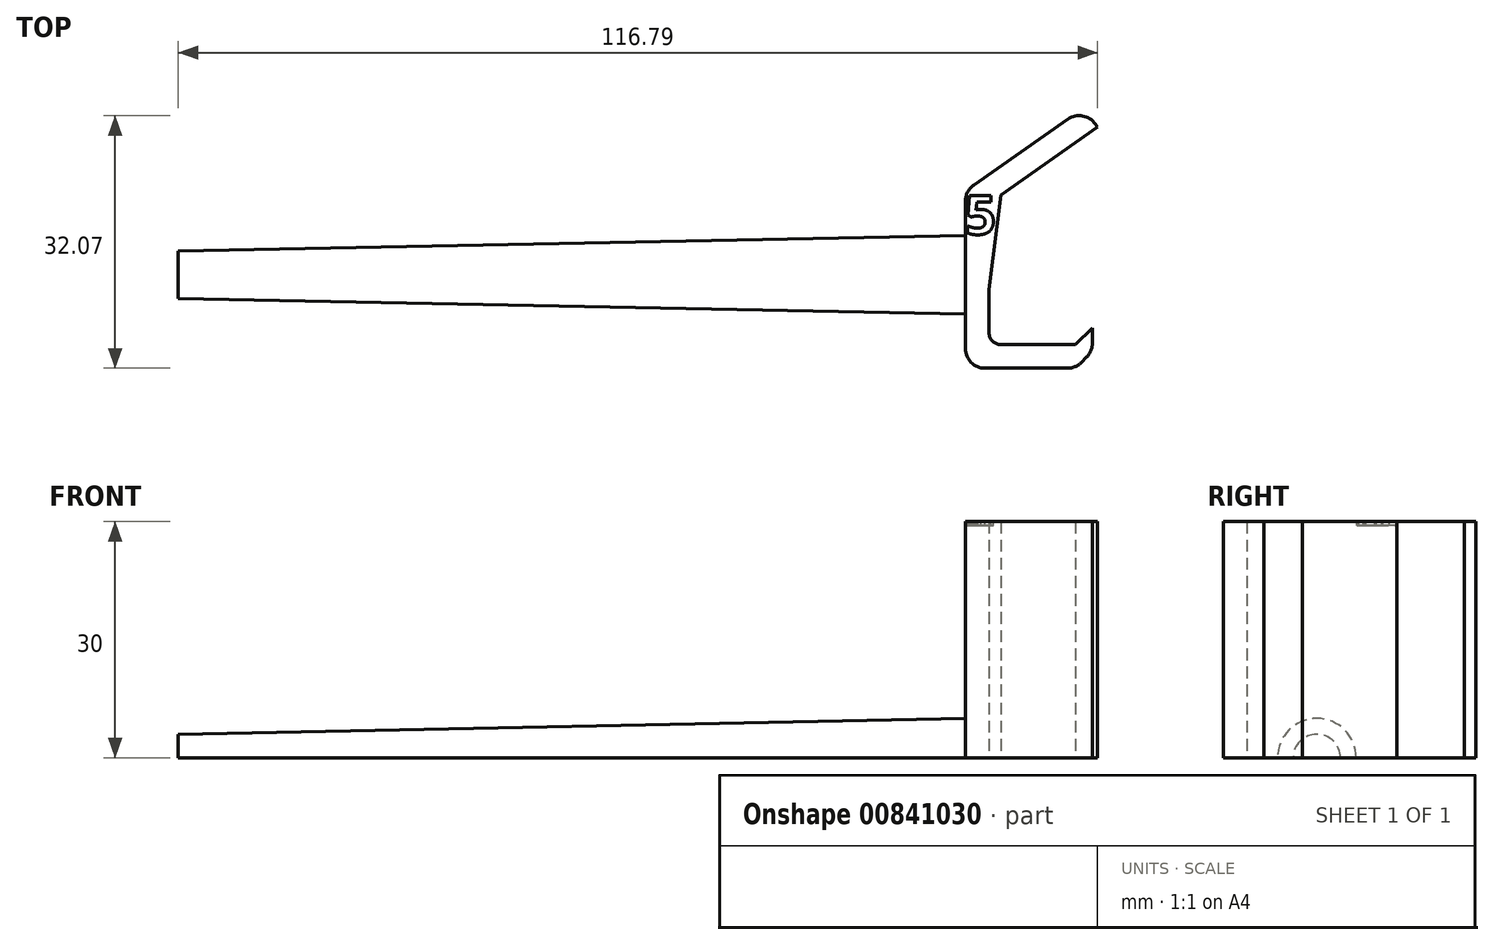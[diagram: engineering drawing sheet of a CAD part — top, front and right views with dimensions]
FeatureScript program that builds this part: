
annotation { "Feature Type Name" : "Feature", "Feature Type Description" : "" }
export const myFeature = defineFeature(function(context is Context, id is Id, definition is map)
    precondition{}
    {
        {
            var Q0;
            Q0=qCreatedBy(makeId("Top.planeOp"),FACE);
            var sketch = newSketch(context, id + "F0", { "sketchPlane" : qUnion([Q0])});
            skLineSegment(sketch, "E0", {"start": v(14, -8.85) * mm, "end": v(4.5, -8.85) * mm});
            skLineSegment(sketch, "E1", {"start": v(4.5, 10.15) * mm, "end": v(16.79, 18.75) * mm});
            skLineSegment(sketch, "E2", {"start": v(16.79, 18.75) * mm, "end": v(16.5, 19.16) * mm});
            skLineSegment(sketch, "E3", {"start": v(13.02, 19.77) * mm, "end": v(1.07, 11.4) * mm});
            skLineSegment(sketch, "E4", {"start": v(0, 9.35) * mm, "end": v(0, -9.35) * mm});
            skLineSegment(sketch, "E5", {"start": v(2.5, -11.85) * mm, "end": v(12.96, -11.85) * mm});
            skLineSegment(sketch, "E6", {"start": v(14.73, -11.12) * mm, "end": v(15.39, -10.47) * mm});
            skLineSegment(sketch, "E7", {"start": v(16.12, -6.73) * mm, "end": v(14, -8.85) * mm});
            skLineSegment(sketch, "E8", {"start": v(16.12, -8.7) * mm, "end": v(16.12, -6.73) * mm});
            skLineSegment(sketch, "E9", {"start": v(3, -7.35) * mm, "end": v(3, -1.85) * mm});
            skLineSegment(sketch, "E10", {"start": v(3, -1.85) * mm, "end": v(4.5, 10.15) * mm});
            skLineSegment(sketch, "E11", {"start": v(-5.47, 10.15) * mm, "end": v(4.5, 10.15) * mm, "construction": true});
            skPoint(sketch, "E12.visualSharp", {"position": v(0, -11.85) * mm});
            skArc(sketch, "E12.filletArc", {"start": v(0, -9.35) * mm, "mid": v(0.73, -11.12) * mm, "end": v(2.5, -11.85) * mm});
            skPoint(sketch, "E13.visualSharp", {"position": v(0, 10.66) * mm});
            skArc(sketch, "E13.filletArc", {"start": v(1.07, 11.4) * mm, "mid": v(0.28, 10.5) * mm, "end": v(0, 9.35) * mm});
            skPoint(sketch, "E14.visualSharp", {"position": v(15.07, 21.2) * mm});
            skArc(sketch, "E14.filletArc", {"start": v(16.5, 19.16) * mm, "mid": v(14.89, 20.19) * mm, "end": v(13.02, 19.77) * mm});
            skPoint(sketch, "E15.visualSharp", {"position": v(14, -11.85) * mm});
            skArc(sketch, "E15.filletArc", {"start": v(12.96, -11.85) * mm, "mid": v(13.92, -11.66) * mm, "end": v(14.73, -11.12) * mm});
            skPoint(sketch, "E16.visualSharp", {"position": v(16.12, -9.73) * mm});
            skArc(sketch, "E16.filletArc", {"start": v(15.39, -10.47) * mm, "mid": v(15.93, -9.65) * mm, "end": v(16.12, -8.7) * mm});
            skPoint(sketch, "E17.visualSharp", {"position": v(3, -8.85) * mm});
            skArc(sketch, "E17.filletArc", {"start": v(3, -7.35) * mm, "mid": v(3.44, -8.42) * mm, "end": v(4.5, -8.85) * mm});
            skPoint(sketch, "E18", {"position": v(0, 0) * mm});
            skSolve(sketch);
        }
        {
            var Q0;
            Q0=makeQuery(id+"F0.imprint","IMPRINT",FACE,{"disambiguationData":[TD([[makeQuery(id+"F0.imprint","IMPRINT",EDGE,{"derivedFrom":sQuery(id+"F0.wireOp",EDGE,"E0")}),1.0]])]});
            extrude(context, id + "F1", {"entities" : qUnion([Q0]), "depth" : 30 * mm, "offsetDistance" : 25 * mm});
        }
        {
            var Q0;
            Q0=makeQuery(id+"F1.opExtrude","CAP_FACE",FACE,{"disambiguationData":[OSD([sQuery(id+"F0.wireOp",EDGE,"E0"),sQuery(id+"F0.wireOp",EDGE,"E1"),sQuery(id+"F0.wireOp",EDGE,"E3"),sQuery(id+"F0.wireOp",EDGE,"E4"),sQuery(id+"F0.wireOp",EDGE,"E5"),sQuery(id+"F0.wireOp",EDGE,"E6"),sQuery(id+"F0.wireOp",EDGE,"E7"),sQuery(id+"F0.wireOp",EDGE,"E8"),sQuery(id+"F0.wireOp",EDGE,"E9"),sQuery(id+"F0.wireOp",EDGE,"E10"),sQuery(id+"F0.wireOp",EDGE,"E12.filletArc"),sQuery(id+"F0.wireOp",EDGE,"E13.filletArc"),sQuery(id+"F0.wireOp",EDGE,"E14.filletArc"),sQuery(id+"F0.wireOp",EDGE,"E15.filletArc"),sQuery(id+"F0.wireOp",EDGE,"E16.filletArc")])],"isStart":false});
            var sketch = newSketch(context, id + "F2", { "sketchPlane" : qUnion([Q0])});
            skText(sketch, "E19", { "text": "5\n", "fontName": "OpenSans-Bold.ttf"});
            const initialGuessF2  = {"E19": [-0.0001, 0.00515, 1, 0, 0.005]};
            skSetInitialGuess(sketch, initialGuessF2);
            skSolve(sketch);
        }
        {
            var Q0;
            Q0 = qSketchRegion(id + "F2", true);
            extrude(context, id + "F3", {"entities" : qUnion([Q0]), "operationType" : NewBodyOperationType.REMOVE, "oppositeDirection" : true, "depth" : 0.5 * mm, "offsetDistance" : 25 * mm});
        }
        {
            var Q0;
            Q0=qCreatedBy(makeId("Front.planeOp"),FACE);
            var sketch = newSketch(context, id + "F4", { "sketchPlane" : qUnion([Q0])});
            skLineSegment(sketch, "E20", {"start": v(0, 0) * mm, "end": v(-100, 0) * mm});
            skLineSegment(sketch, "E21", {"start": v(-100, 0) * mm, "end": v(-100, 3) * mm});
            skLineSegment(sketch, "E22", {"start": v(-100, 3) * mm, "end": v(0, 5) * mm});
            skLineSegment(sketch, "E23", {"start": v(0, 5) * mm, "end": v(0, 0) * mm});
            skSolve(sketch);
        }
        {
            var Q0;
            Q0 = qSketchRegion(id + "F4", true);
            var Q1;
            Q1=sQuery(id+"F4.wireOp",EDGE,"E20");
            revolve(context, id + "F5", {"operationType" : NewBodyOperationType.ADD, "surfaceOperationType" : NewSurfaceOperationType.NEW, "entities" : qUnion([Q0]), "axis" : qUnion([Q1]), "revolveType" : RevolveType.TWO_DIRECTIONS, "angle" : 90 * degree, "angleBack" : 270 * degree});
        }
    });
